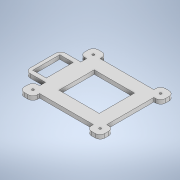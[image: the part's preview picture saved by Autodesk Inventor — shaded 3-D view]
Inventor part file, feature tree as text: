
AUTODESK INVENTOR PART (.ipt)
format: ipt  version: 2020 (Build 240168000, 168)  size: 206,848 bytes
history: native  units: in
note: dims shown in document units (in); Inventor stores cm internally (conversion verified against a paired STEP export)
features: extrude x1, fillet x1, sketch x1
ambient origin geometry x8: Origin, YZ Plane, XZ Plane, XY Plane, X Axis, Y Axis, Z Axis, Center Point
bodies: Body1 (feature_tree)
feature tree (3):
  extrude  "Extrusion3"  Depth=1.718in TaperAngle=360.0deg
  fillet  "Fillet4"  Radius=0.7874in
  sketch  "Sketch1"  dims[d2=0.344in d4=0.7874in d6=360.0deg d8=0.7874in d10=360.0deg d19=0.228in d20=0.228in d21=0.5154in d29=0.055in d30=0.7874in d32=360.0deg d34=0.1in d35=0.0in d36=0.125in d38=1.718in]
